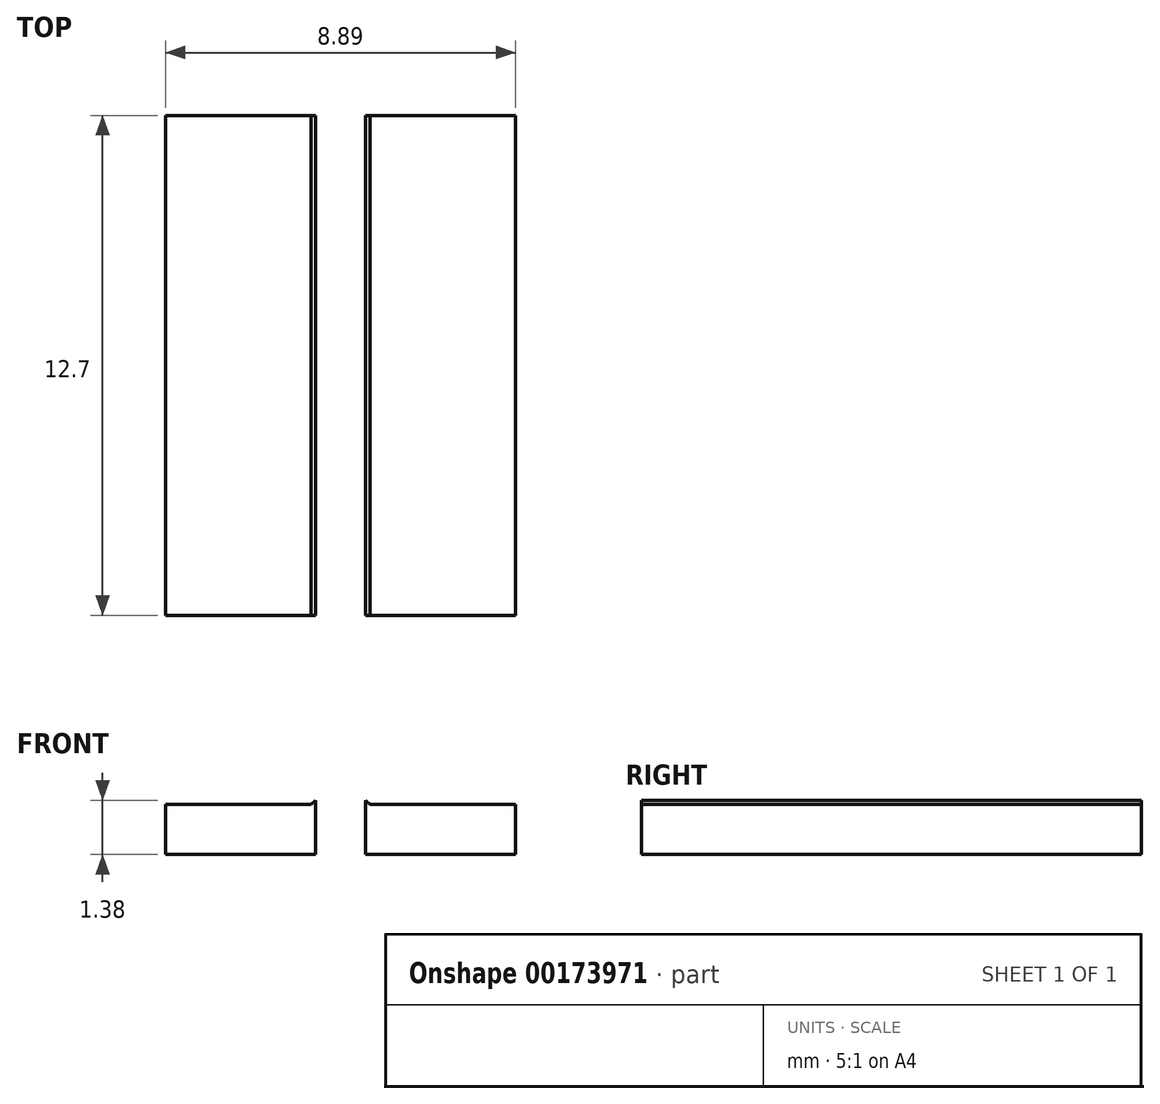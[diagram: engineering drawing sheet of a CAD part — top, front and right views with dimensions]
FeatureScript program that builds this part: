
annotation { "Feature Type Name" : "Feature", "Feature Type Description" : "" }
export const myFeature = defineFeature(function(context is Context, id is Id, definition is map)
    precondition{}
    {
        {
            var Q0;
            Q0=qCreatedBy(makeId("Front.planeOp"),FACE);
            var sketch = newSketch(context, id + "F0", { "sketchPlane" : qUnion([Q0])});
            skLineSegment(sketch, "E0", {"start": v(0, 0) * mm, "end": v(3.81, 0) * mm});
            skLineSegment(sketch, "E1", {"start": v(3.81, 0) * mm, "end": v(3.81, 1.27) * mm});
            skLineSegment(sketch, "E2", {"start": v(3.81, 1.27) * mm, "end": v(0.12, 1.27) * mm});
            skCircle(sketch, "E3", {"center": v(-0.64, 1.27) * mm, "radius": 0.25 * mm});
            skCircle(sketch, "E4", {"center": v(-0.64, 1.27) * mm, "radius": 0.5 * mm});
            skLineSegment(sketch, "E5", {"start": v(0, 0) * mm, "end": v(-0.98, 0.9) * mm});
            skLineSegment(sketch, "E6", {"start": v(0.12, 1.27) * mm, "end": v(-0.3, 1.64) * mm});
            skSolve(sketch);
        }
        {
            var Q0;
            Q0=makeQuery(id+"F0.imprint","IMPRINT",FACE,{"disambiguationData":[TD([[makeQuery(id+"F0.imprint","IMPRINT",EDGE,{"derivedFrom":sQuery(id+"F0.wireOp",EDGE,"E0")}),1.0]])]});
            var Q1;
            Q1=makeQuery(id+"F0.imprint","IMPRINT",FACE,{"disambiguationData":[TD([[makeQuery(id+"F0.imprint","IMPRINT",EDGE,{"derivedFrom":sQuery(id+"F0.wireOp",EDGE,"E3")}),-1.0]])]});
            extrude(context, id + "F1", {"entities" : qUnion([Q0, Q1]), "endBound" : BoundingType.SYMMETRIC, "depth" : 12.7 * mm});
        }
        {
            var Q0;
            Q0=qCreatedBy(makeId("Front.planeOp"),FACE);
            var sketch = newSketch(context, id + "F2", { "sketchPlane" : qUnion([Q0])});
            skLineSegment(sketch, "E7.0.0", {"start": v(-0.98, 0.9) * mm, "end": v(0, 0) * mm, "construction": true});
            skLineSegment(sketch, "E7.0.1", {"start": v(0, 0) * mm, "end": v(3.81, 0) * mm, "construction": true});
            skLineSegment(sketch, "E7.0.2", {"start": v(3.81, 0) * mm, "end": v(3.81, 1.27) * mm, "construction": true});
            skLineSegment(sketch, "E7.0.3", {"start": v(3.81, 1.27) * mm, "end": v(0.12, 1.27) * mm, "construction": true});
            skLineSegment(sketch, "E7.0.4", {"start": v(0.12, 1.27) * mm, "end": v(-0.3, 1.64) * mm, "construction": true});
            skArc(sketch, "E7.0.5", {"start": v(-0.3, 1.64) * mm, "mid": v(-1, 1.61) * mm, "end": v(-0.98, 0.9) * mm, "construction": true});
            skCircle(sketch, "E8.0", {"center": v(-0.64, 1.27) * mm, "radius": 0.25 * mm});
            skLineSegment(sketch, "E9", {"start": v(-0.64, 1.27) * mm, "end": v(-0.64, 0) * mm, "construction": true});
            skLineSegment(sketch, "E10.MirrorCS", {"start": v(-0.3, 0.9) * mm, "end": v(-1.27, 0) * mm});
            skLineSegment(sketch, "E11.MirrorCS", {"start": v(-1.39, 1.27) * mm, "end": v(-0.98, 1.64) * mm});
            skArc(sketch, "E12.MirrorCS", {"start": v(-0.98, 1.64) * mm, "mid": v(-0.26, 1.61) * mm, "end": v(-0.3, 0.9) * mm});
            skLineSegment(sketch, "E13.MirrorCS", {"start": v(-1.27, 0) * mm, "end": v(-5.08, 0) * mm});
            skLineSegment(sketch, "E14.MirrorCS", {"start": v(-5.08, 1.27) * mm, "end": v(-1.39, 1.27) * mm});
            skLineSegment(sketch, "E15.MirrorCS", {"start": v(-5.08, 0) * mm, "end": v(-5.08, 1.27) * mm});
            skSolve(sketch);
        }
        {
            var Q0;
            Q0 = qSketchRegion(id + "F2", true);
            extrude(context, id + "F3", {"entities" : qUnion([Q0]), "endBound" : BoundingType.SYMMETRIC, "depth" : 12.7 * mm});
        }
        {
            var Q0;
            Q0=qCreatedBy(makeId("Top.planeOp"),FACE);
            var sketch = newSketch(context, id + "F4", { "sketchPlane" : qUnion([Q0])});
            skLineSegment(sketch, "E16.bottom", {"start": v(-1.27, 2.54) * mm, "end": v(0, 2.54) * mm});
            skLineSegment(sketch, "E16.top", {"start": v(-1.27, -2.54) * mm, "end": v(0, -2.54) * mm});
            skLineSegment(sketch, "E16.left", {"start": v(-1.27, 2.54) * mm, "end": v(-1.27, -2.54) * mm});
            skLineSegment(sketch, "E16.right", {"start": v(0, 2.54) * mm, "end": v(0, -2.54) * mm});
            skPoint(sketch, "E16.middle", {"position": v(-0.64, 0) * mm});
            skLineSegment(sketch, "E17.0", {"start": v(-0.38, 6.35) * mm, "end": v(-0.89, 6.35) * mm, "construction": true});
            skLineSegment(sketch, "E18.0", {"start": v(-0.38, -6.35) * mm, "end": v(-0.89, -6.35) * mm, "construction": true});
            skLineSegment(sketch, "E19", {"start": v(-0.64, -6.35) * mm, "end": v(-0.64, 6.35) * mm, "construction": true});
            skLineSegment(sketch, "E20", {"start": v(-1.27, -2.54) * mm, "end": v(-1.27, -8.9) * mm});
            skLineSegment(sketch, "E21", {"start": v(-1.27, -8.9) * mm, "end": v(0, -8.9) * mm});
            skLineSegment(sketch, "E22", {"start": v(0, -8.9) * mm, "end": v(0, -2.54) * mm});
            skLineSegment(sketch, "E23", {"start": v(-1.27, 2.54) * mm, "end": v(-1.27, 8.9) * mm});
            skLineSegment(sketch, "E24", {"start": v(-1.27, 8.9) * mm, "end": v(0, 8.9) * mm});
            skLineSegment(sketch, "E25", {"start": v(0, 8.9) * mm, "end": v(0, 2.54) * mm});
            skSolve(sketch);
        }
        {
            var Q0;
            Q0=makeQuery(id+"F4.imprint","IMPRINT",FACE,{"disambiguationData":[TD([[makeQuery(id+"F4.imprint","IMPRINT",EDGE,{"derivedFrom":sQuery(id+"F4.wireOp",EDGE,"E16.bottom")}),-1.0]])]});
            extrude(context, id + "F5", {"entities" : qUnion([Q0]), "operationType" : NewBodyOperationType.REMOVE, "endBound" : BoundingType.THROUGH_ALL, "depth" : 25.4 * mm});
        }
        {
            var Q0;
            Q0=makeQuery(id+"F4.imprint","IMPRINT",FACE,{"disambiguationData":[TD([[makeQuery(id+"F4.imprint","IMPRINT",EDGE,{"derivedFrom":sQuery(id+"F4.wireOp",EDGE,"E16.bottom")}),1.0]])]});
            var Q1;
            Q1=makeQuery(id+"F4.imprint","IMPRINT",FACE,{"disambiguationData":[TD([[makeQuery(id+"F4.imprint","IMPRINT",EDGE,{"derivedFrom":sQuery(id+"F4.wireOp",EDGE,"E16.top")}),-1.0]])]});
            extrude(context, id + "F6", {"entities" : qUnion([Q0, Q1]), "operationType" : NewBodyOperationType.REMOVE, "endBound" : BoundingType.THROUGH_ALL, "depth" : 25.4 * mm});
        }
    });
